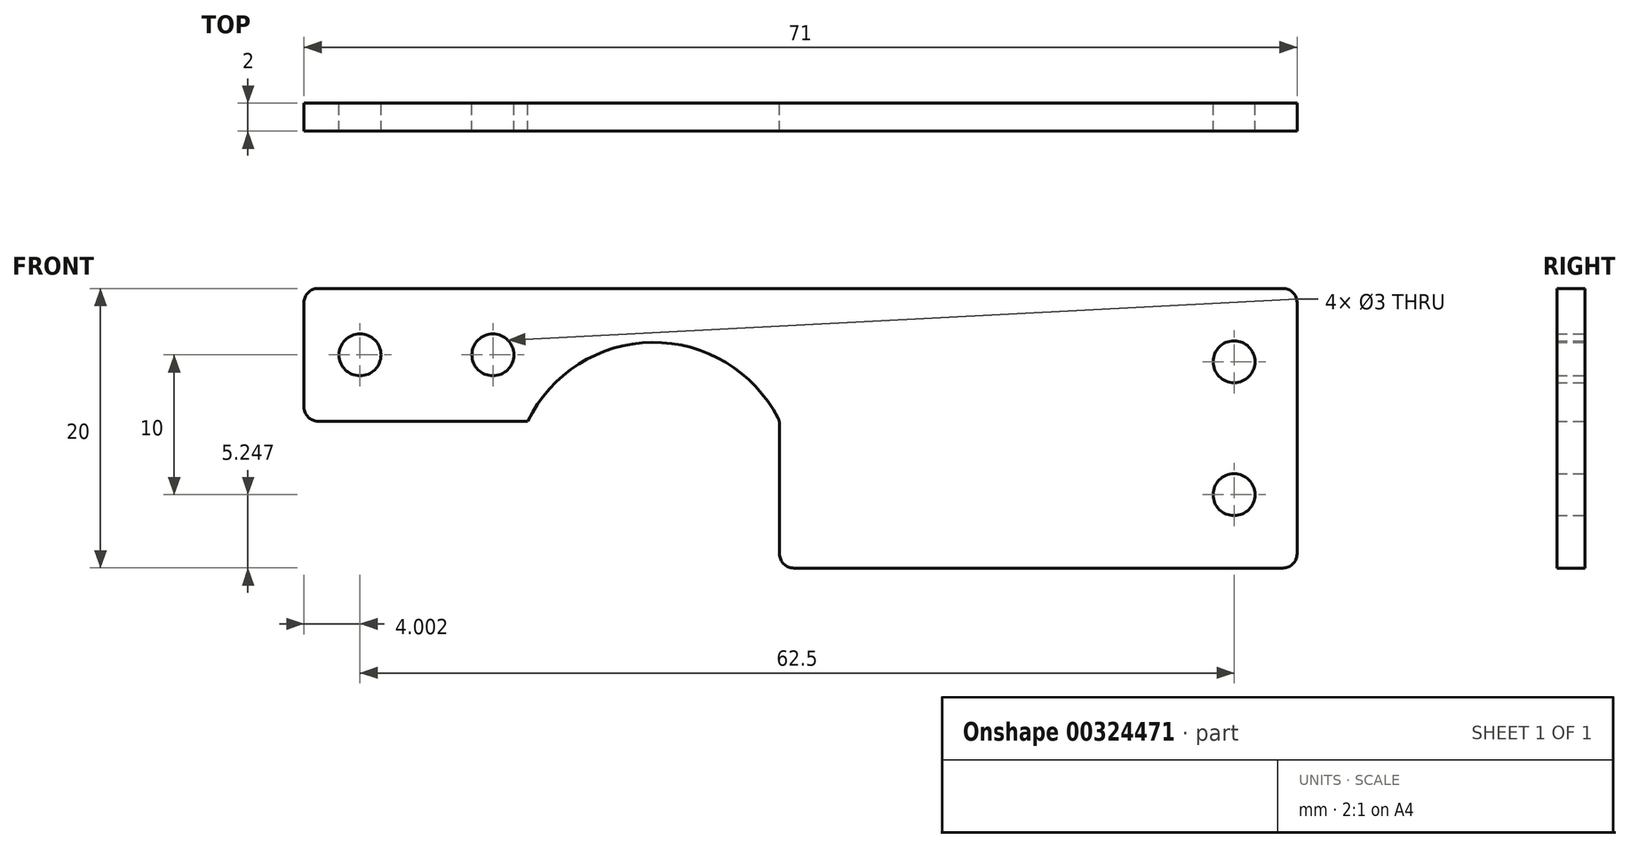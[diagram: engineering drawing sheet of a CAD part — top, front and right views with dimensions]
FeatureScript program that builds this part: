
annotation { "Feature Type Name" : "Feature", "Feature Type Description" : "" }
export const myFeature = defineFeature(function(context is Context, id is Id, definition is map)
    precondition{}
    {
        {
            var Q0;
            Q0=qCreatedBy(makeId("Front.planeOp"),FACE);
            var sketch = newSketch(context, id + "F0", { "sketchPlane" : qUnion([Q0])});
            skLineSegment(sketch, "E0", {"start": v(46.64, 11.12) * mm, "end": v(46.64, -8.88) * mm});
            skLineSegment(sketch, "E1", {"start": v(46.64, -8.88) * mm, "end": v(9.64, -8.88) * mm});
            skLineSegment(sketch, "E2", {"start": v(-8.36, 1.62) * mm, "end": v(-24.36, 1.62) * mm});
            skLineSegment(sketch, "E3", {"start": v(46.64, 11.12) * mm, "end": v(-24.36, 11.12) * mm});
            skLineSegment(sketch, "E4", {"start": v(-24.36, 11.12) * mm, "end": v(-24.36, 1.62) * mm});
            skArc(sketch, "E5", {"start": v(9.64, 1.62) * mm, "mid": v(0.64, 7.26) * mm, "end": v(-8.36, 1.62) * mm});
            skLineSegment(sketch, "E6", {"start": v(9.64, 1.62) * mm, "end": v(9.64, -8.88) * mm});
            skLineSegment(sketch, "E7", {"start": v(-20.36, 11.12) * mm, "end": v(-20.36, 1.62) * mm, "construction": true});
            skLineSegment(sketch, "E8", {"start": v(-10.86, 11.12) * mm, "end": v(-10.86, 1.62) * mm, "construction": true});
            skLineSegment(sketch, "E9", {"start": v(42.14, 11.12) * mm, "end": v(42.14, -8.88) * mm, "construction": true});
            skLineSegment(sketch, "E10", {"start": v(42.14, 5.87) * mm, "end": v(46.64, 5.87) * mm, "construction": true});
            skLineSegment(sketch, "E11", {"start": v(42.14, -3.63) * mm, "end": v(46.64, -3.63) * mm, "construction": true});
            skLineSegment(sketch, "E12", {"start": v(-20.36, 6.37) * mm, "end": v(-10.86, 6.37) * mm, "construction": true});
            skCircle(sketch, "E13", {"center": v(-20.36, 6.37) * mm, "radius": 1.5 * mm});
            skCircle(sketch, "E14", {"center": v(-10.86, 6.37) * mm, "radius": 1.5 * mm});
            skCircle(sketch, "E15", {"center": v(42.14, 5.87) * mm, "radius": 1.5 * mm});
            skCircle(sketch, "E16", {"center": v(42.14, -3.63) * mm, "radius": 1.5 * mm});
            skSolve(sketch);
        }
        {
            var Q0;
            Q0 = qSketchRegion(id + "F0", true);
            extrude(context, id + "F1", {"entities" : qUnion([Q0]), "depth" : 2 * mm});
        }
        {
            var Q0;
            Q0=makeQuery(id+"F1.opExtrude","SWEPT_EDGE",EDGE,{"disambiguationData":[OSD([sQuery(id+"F0.wireOp",EDGE,"E5"),sQuery(id+"F0.wireOp",EDGE,"E6")])]});
            fillet(context, id + "F2", {"entities" : qUnion([Q0]), "radius" : 1 * mm, "tangentPropagation" : true, "allowEdgeOverflow" : false});
        }
        {
            var Q0;
            Q0=makeQuery(id+"F1.opExtrude","SWEPT_EDGE",EDGE,{"disambiguationData":[OSD([sQuery(id+"F0.wireOp",EDGE,"E0"),sQuery(id+"F0.wireOp",EDGE,"E3")])]});
            var Q1;
            Q1=makeQuery(id+"F1.opExtrude","SWEPT_EDGE",EDGE,{"disambiguationData":[OSD([sQuery(id+"F0.wireOp",EDGE,"E3"),sQuery(id+"F0.wireOp",EDGE,"E4")])]});
            var Q2;
            Q2=makeQuery(id+"F1.opExtrude","SWEPT_EDGE",EDGE,{"disambiguationData":[OSD([sQuery(id+"F0.wireOp",EDGE,"E2"),sQuery(id+"F0.wireOp",EDGE,"E4")])]});
            var Q3;
            Q3=makeQuery(id+"F1.opExtrude","SWEPT_EDGE",EDGE,{"disambiguationData":[OSD([sQuery(id+"F0.wireOp",EDGE,"E1"),sQuery(id+"F0.wireOp",EDGE,"E6")])]});
            var Q4;
            Q4=makeQuery(id+"F1.opExtrude","SWEPT_EDGE",EDGE,{"disambiguationData":[OSD([sQuery(id+"F0.wireOp",EDGE,"E0"),sQuery(id+"F0.wireOp",EDGE,"E1")])]});
            fillet(context, id + "F3", {"entities" : qUnion([Q0, Q1, Q2, Q3, Q4]), "radius" : 1 * mm, "tangentPropagation" : true, "allowEdgeOverflow" : false});
        }
    });
